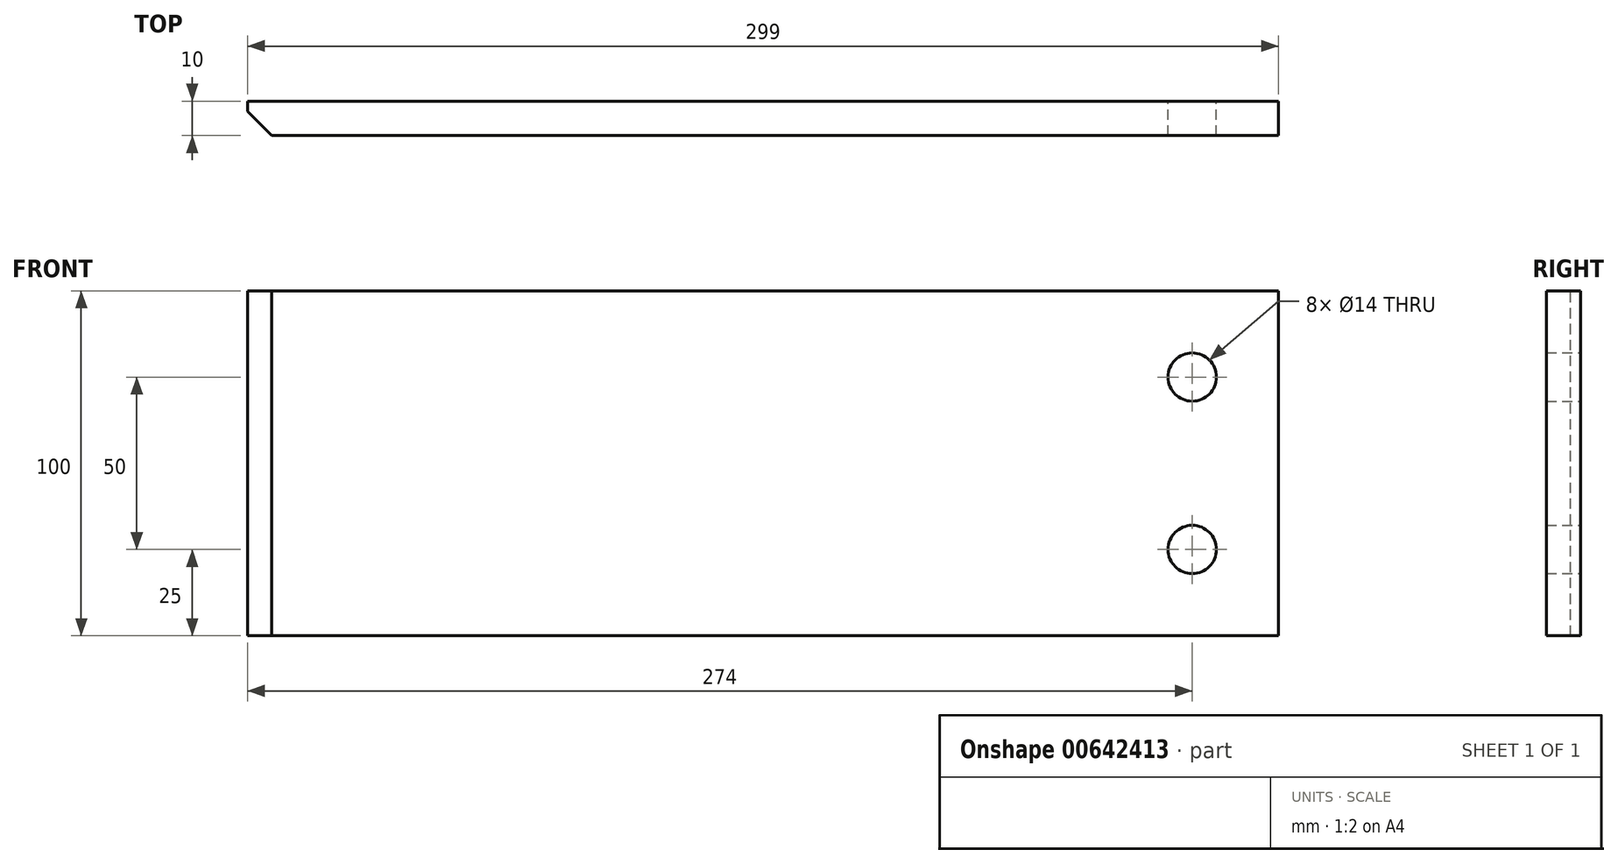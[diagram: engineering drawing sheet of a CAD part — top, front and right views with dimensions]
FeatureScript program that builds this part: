
annotation { "Feature Type Name" : "Feature", "Feature Type Description" : "" }
export const myFeature = defineFeature(function(context is Context, id is Id, definition is map)
    precondition{}
    {
        {
            var Q0;
            Q0=qCreatedBy(makeId("Front.planeOp"),FACE);
            var sketch = newSketch(context, id + "F0", { "sketchPlane" : qUnion([Q0])});
            skLineSegment(sketch, "E0.bottom", {"start": v(149.5, -50) * mm, "end": v(-149.5, -50) * mm});
            skLineSegment(sketch, "E0.top", {"start": v(149.5, 50) * mm, "end": v(-149.5, 50) * mm});
            skLineSegment(sketch, "E0.left", {"start": v(149.5, -50) * mm, "end": v(149.5, 50) * mm});
            skLineSegment(sketch, "E0.right", {"start": v(-149.5, -50) * mm, "end": v(-149.5, 50) * mm});
            skPoint(sketch, "E0.middle", {"position": v(0, 0) * mm});
            skCircle(sketch, "E1", {"center": v(124.5, 25) * mm, "radius": 7 * mm});
            skCircle(sketch, "E2", {"center": v(124.5, -25) * mm, "radius": 7 * mm});
            skSolve(sketch);
        }
        {
            var Q0;
            Q0=makeQuery(id+"F0.imprint","IMPRINT",FACE,{"disambiguationData":[TD([[makeQuery(id+"F0.imprint","IMPRINT",EDGE,{"derivedFrom":sQuery(id+"F0.wireOp",EDGE,"E0.bottom")}),-1.0]])]});
            extrude(context, id + "F1", {"entities" : qUnion([Q0]), "depth" : 10 * mm, "offsetDistance" : 25 * mm});
        }
        {
            var Q0;
            Q0=makeQuery(id+"F1.opExtrude","CAP_EDGE",EDGE,{"disambiguationData":[OSD([sQuery(id+"F0.wireOp",EDGE,"E0.right")])],"isStart":false});
            chamfer(context, id + "F2", {"entities" : qUnion([Q0]), "width" : 7 * mm, "tangentPropagation" : true});
        }
    });
